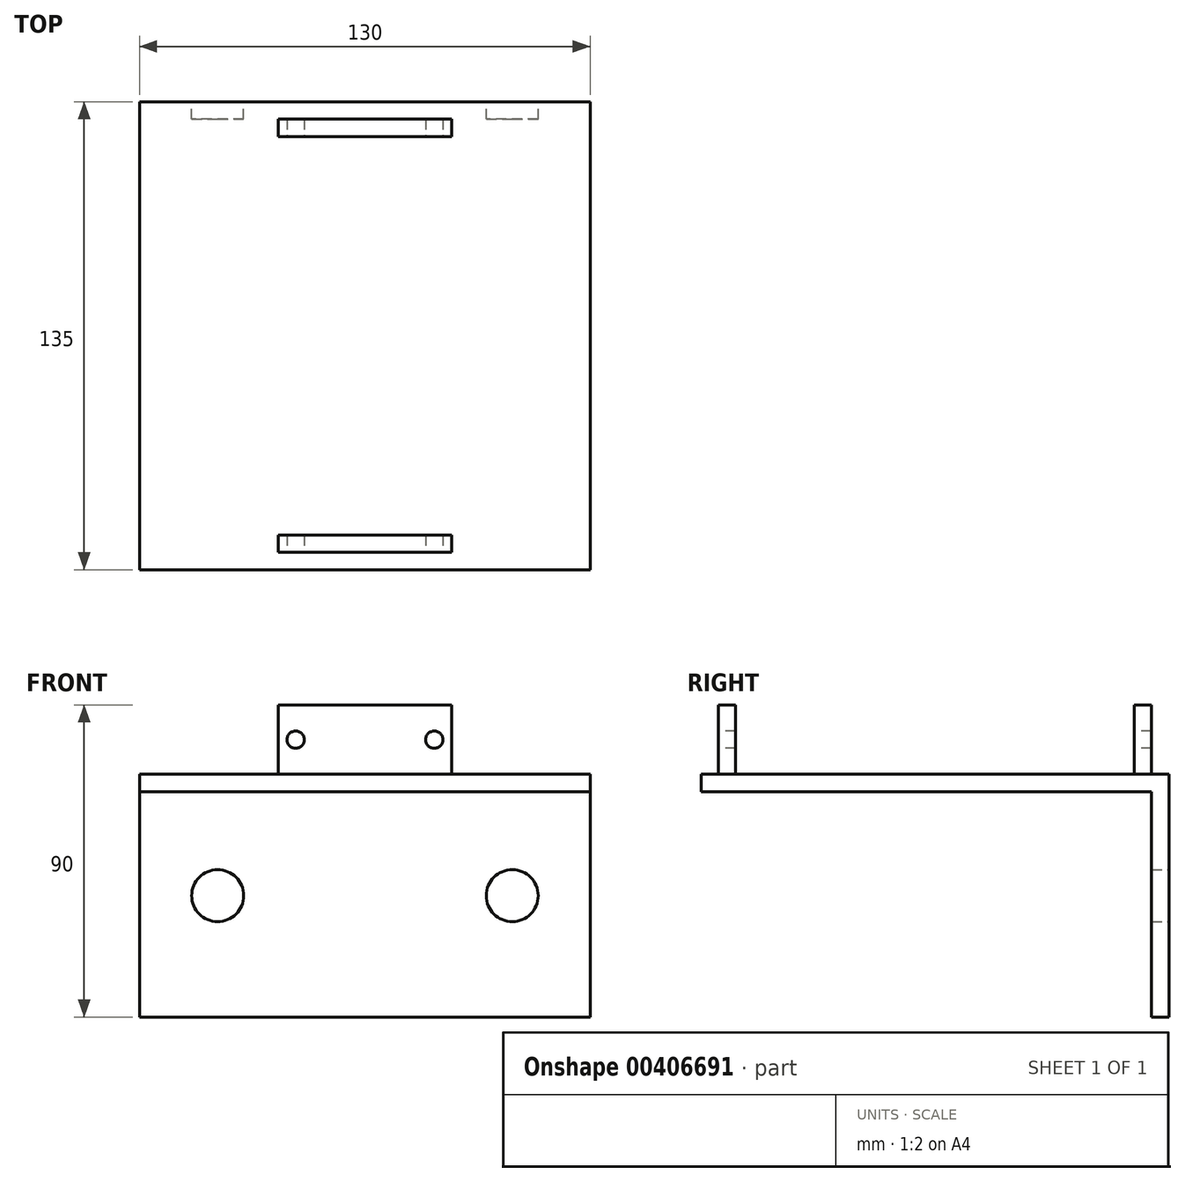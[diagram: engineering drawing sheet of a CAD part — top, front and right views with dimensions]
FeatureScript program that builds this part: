
annotation { "Feature Type Name" : "Feature", "Feature Type Description" : "" }
export const myFeature = defineFeature(function(context is Context, id is Id, definition is map)
    precondition{}
    {
        {
            var Q0;
            Q0=qCreatedBy(makeId("Front.planeOp"),FACE);
            var sketch = newSketch(context, id + "F0", { "sketchPlane" : qUnion([Q0])});
            skLineSegment(sketch, "E0", {"start": v(0, 0) * mm, "end": v(0, 70) * mm});
            skLineSegment(sketch, "E1", {"start": v(0, 70) * mm, "end": v(130, 70) * mm});
            skLineSegment(sketch, "E2", {"start": v(130, 70) * mm, "end": v(130, 0) * mm});
            skLineSegment(sketch, "E3", {"start": v(130, 0) * mm, "end": v(0, 0) * mm});
            skCircle(sketch, "E4", {"center": v(107.5, 35) * mm, "radius": 7.5 * mm});
            skCircle(sketch, "E5", {"center": v(22.5, 35) * mm, "radius": 7.5 * mm});
            skPoint(sketch, "E6.orphan", {"position": v(130, 35) * mm});
            skPoint(sketch, "E7.orphan", {"position": v(0, 35) * mm});
            skSolve(sketch);
        }
        {
            var Q0;
            Q0 = qSketchRegion(id + "F0", true);
            extrude(context, id + "F1", {"entities" : qUnion([Q0]), "depth" : 5 * mm});
        }
        {
            var Q0;
            Q0=makeQuery(id+"F1.opExtrude","CAP_FACE",FACE,{"disambiguationData":[OSD([sQuery(id+"F0.wireOp",EDGE,"E0"),sQuery(id+"F0.wireOp",EDGE,"E1"),sQuery(id+"F0.wireOp",EDGE,"E2"),sQuery(id+"F0.wireOp",EDGE,"E3"),sQuery(id+"F0.wireOp",EDGE,"E4"),sQuery(id+"F0.wireOp",EDGE,"E5")])],"isStart":false});
            var sketch = newSketch(context, id + "F2", { "sketchPlane" : qUnion([Q0])});
            skLineSegment(sketch, "E8", {"start": v(0, 70) * mm, "end": v(0, 65) * mm});
            skLineSegment(sketch, "E9", {"start": v(0, 65) * mm, "end": v(130, 65) * mm});
            skLineSegment(sketch, "E10", {"start": v(130, 65) * mm, "end": v(130, 70) * mm});
            skLineSegment(sketch, "E11", {"start": v(130, 70) * mm, "end": v(0, 70) * mm});
            skSolve(sketch);
        }
        {
            var Q0;
            Q0 = qSketchRegion(id + "F2", true);
            extrude(context, id + "F3", {"entities" : qUnion([Q0]), "operationType" : NewBodyOperationType.ADD, "depth" : 130 * mm});
        }
        {
            var Q0;
            Q0=makeQuery(id+"F3.boolean.opBoolean","MERGE",FACE,{"derivedFrom":[makeQuery(id+"F1.opExtrude","SWEPT_FACE",FACE,{"disambiguationData":[OSD([sQuery(id+"F0.wireOp",EDGE,"E1")])]}),makeQuery(id+"F3.opExtrude","SWEPT_FACE",FACE,{"disambiguationData":[OSD([sQuery(id+"F2.wireOp",EDGE,"E11")])]})]});
            var sketch = newSketch(context, id + "F4", { "sketchPlane" : qUnion([Q0])});
            skLineSegment(sketch, "E12", {"start": v(40, -130) * mm, "end": v(90, -130) * mm});
            skLineSegment(sketch, "E13", {"start": v(90, -5) * mm, "end": v(40, -5) * mm});
            skPoint(sketch, "E14.endSnap0", {"position": v(65, -135) * mm});
            skLineSegment(sketch, "E15", {"start": v(65, 0) * mm, "end": v(90, 0) * mm});
            skLineSegment(sketch, "E16", {"start": v(90, -5) * mm, "end": v(90, -10) * mm});
            skLineSegment(sketch, "E17", {"start": v(40, -130) * mm, "end": v(40, -125) * mm});
            skLineSegment(sketch, "E18", {"start": v(40, -125) * mm, "end": v(90, -125) * mm});
            skLineSegment(sketch, "E19", {"start": v(40, -5) * mm, "end": v(40, -10) * mm});
            skLineSegment(sketch, "E20", {"start": v(40, -10) * mm, "end": v(90, -10) * mm});
            skLineSegment(sketch, "E21.trimOffspring", {"start": v(40, -10) * mm, "end": v(40, -5) * mm});
            skLineSegment(sketch, "E22.trimOffspring", {"start": v(90, -125) * mm, "end": v(90, -130) * mm});
            skPoint(sketch, "E23.trimOffspring.end.orphan", {"position": v(65, -141.03) * mm});
            skSolve(sketch);
        }
        {
            var Q0;
            Q0 = qSketchRegion(id + "F4", true);
            extrude(context, id + "F5", {"entities" : qUnion([Q0]), "operationType" : NewBodyOperationType.ADD, "depth" : 20 * mm});
        }
        {
            var Q0;
            Q0=makeQuery(id+"F5.opExtrude","SWEPT_FACE",FACE,{"disambiguationData":[OSD([sQuery(id+"F4.wireOp",EDGE,"E12")])]});
            var sketch = newSketch(context, id + "F6", { "sketchPlane" : qUnion([Q0])});
            skLineSegment(sketch, "E24", {"start": v(90, 70) * mm, "end": v(90, 90) * mm});
            skLineSegment(sketch, "E25", {"start": v(40, 70) * mm, "end": v(40, 80) * mm});
            skLineSegment(sketch, "E26", {"start": v(65, 90) * mm, "end": v(85, 90) * mm});
            skLineSegment(sketch, "E27", {"start": v(65, 90) * mm, "end": v(45, 90) * mm});
            skCircle(sketch, "E28", {"center": v(45, 80) * mm, "radius": 2.5 * mm});
            skCircle(sketch, "E29", {"center": v(85, 80) * mm, "radius": 2.5 * mm});
            skSolve(sketch);
        }
        {
            var Q0;
            Q0 = qSketchRegion(id + "F6", true);
            extrude(context, id + "F7", {"entities" : qUnion([Q0]), "operationType" : NewBodyOperationType.REMOVE, "endBound" : BoundingType.THROUGH_ALL, "oppositeDirection" : true, "depth" : 25 * mm});
        }
    });
